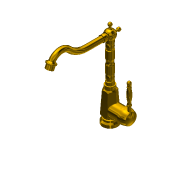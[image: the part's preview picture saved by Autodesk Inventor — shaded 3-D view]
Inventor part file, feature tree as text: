
AUTODESK INVENTOR PART (.ipt)
format: ipt  version: 2018 (Build 220112000, 112)  size: 729,088 bytes
history: native  units: mm
features: sketch x31, extrude x17, projected_geometry x12, fillet x9, revolve x9, plane x6, chamfer x4, other x3, sweep x1, loft x1
ambient origin geometry x8: Origin, YZ Plane, XZ Plane, XY Plane, X Axis, Y Axis, Z Axis, Center Point
bodies: Solid1 (feature_tree)
feature tree (93):
  sweep  "Sweep1"
  extrude  "Extrusion1"  Depth=35.0mm
  extrude  "Extrusion2"  TaperAngle=0.0deg  [1 undecoded]
  fillet  "Fillet1"  Radius=22.8mm
  chamfer  "Chamfer1"  Distance=13.0mm
  extrude  "Extrusion3"  Depth=3.0mm TaperAngle=0.0deg
  extrude  "Extrusion4"  Depth=3.0mm TaperAngle=45.0deg
  revolve  "Revolution1"  [1 undecoded]
  revolve  "Revolution2"  [1 undecoded]
  plane  "Work Plane2"
  extrude  "Extrusion5"  TaperAngle=90.0deg  [1 undecoded]
  other  "Work Axis1"
  sketch  "Sketch10"  dims[d35=1.0mm d36=2.0mm]
  plane  "Work Plane4"
  extrude  "Extrusion6"  Depth=1.0mm
  other  "Work Axis2"
  revolve  "Revolution3"  [1 undecoded]
  revolve  "Revolution4"  Angle=90.0deg
  revolve  "Revolution5"  [1 undecoded]
  fillet  "Fillet2"  [1 undecoded]
  revolve  "Revolution6"  [1 undecoded]
  fillet  "Fillet3"  [1 undecoded]
  extrude  "Extrusion7"  TaperAngle=90.0deg  [1 undecoded]
  revolve  "Revolution7"  Angle=90.0deg
  fillet  "Fillet4"  Radius=6.0mm
  extrude  "Extrusion8"  Depth=12.0mm
  extrude  "Extrusion13"  Depth=6.0mm
  sketch  "Sketch19"  dims[d57=90.0deg d58=2.0mm]
  plane  "Work Plane5"
  loft  "Loft1"
  chamfer  "Chamfer2"  Distance=1.0mm
  fillet  "Fillet5"  Radius=29.0mm
  extrude  "Extrusion10"  Depth=3.0mm TaperAngle=0.0deg
  extrude  "Extrusion11"  Depth=3.0mm
  extrude  "Extrusion12"  Depth=3.0mm
  chamfer  "Chamfer3"  Distance=42.0mm
  chamfer  "Chamfer4"  Angle=90.0deg  [1 undecoded]
  fillet  "Fillet6"  [1 undecoded]
  extrude  "Extrusion14"  Depth=3.0mm TaperAngle=45.0deg
  fillet  "Fillet7"  Radius=1.0mm
  extrude  "Extrusion15"  Depth=3.0mm
  extrude  "Extrusion16"  Depth=10.0mm TaperAngle=0.0deg
  other  "Work Axis3"
  sketch  "Sketch28"  dims[d70=30.0mm]
  plane  "Work Plane6"
  revolve  "Revolution8"  [1 undecoded]
  revolve  "Revolution9"  [1 undecoded]
  extrude  "Extrusion17"  Depth=3.0mm
  fillet  "Fillet8"  Radius=13.0mm
  fillet  "Fillet9"  Radius=6.5mm
  extrude  "Extrusion18"  Depth=3.0mm TaperAngle=45.0deg
  sketch  "Sketch1"  dims[d0=50.0mm d1=15.0mm]
  sketch  "Sketch2"  dims[d5=170.0mm d10=35.0mm]
  sketch  "Sketch3"  dims[d11=17.5mm d12=0.0mm d13=0.0mm d14=22.8mm d15=13.0mm d16=0.0mm]
  sketch  "Sketch4"  dims[d17=3.0mm d18=5.0mm d19=0.0mm]
  sketch  "Sketch5"  dims[d20=2.0mm d21=3.0mm d22=2.0mm d23=45.0deg]
  projected_geometry  "Projected Loop1"
  sketch  "Sketch6"  dims[d24=1.0mm d25=5.0mm d26=0.0mm]
  sketch  "Sketch7"  dims[d27=23.0mm d28=16.0mm d29=0.0mm]
  projected_geometry  "Projected Loop2"
  sketch  "Sketch8"  dims[d30=2.0mm d32=90.0deg]
  plane  "Work Plane1"
  sketch  "Sketch9"  dims[d33=2.0mm d34=1.0mm]
  plane  "Work Plane3"
  sketch  "Sketch11"  dims[d37=32.0mm d38=90.0deg]
  sketch  "Sketch12"  dims[d39=-2.0mm d40=16.0mm d41=0.0mm d42=0.0mm]
  projected_geometry  "Projected Loop3"
  projected_geometry  "Projected Loop4"
  sketch  "Sketch13"  dims[d43=12.0mm d44=28.0mm d46=-30.0mm]
  sketch  "Sketch14"  dims[d47=16.0mm d48=0.0mm d49=90.0deg]
  projected_geometry  "Projected Loop5"
  projected_geometry  "Projected Loop6"
  sketch  "Sketch15"  dims[d50=1.0mm d51=90.0deg d52=6.0mm]
  sketch  "Sketch16"  dims[d53=0.0mm d54=12.0mm]
  projected_geometry  "Projected Loop7"
  sketch  "Sketch17"  dims[d55=28.0mm d56=6.0mm]
  sketch  "Sketch20"  dims[d59=1.0mm]
  sketch  "Sketch21"  dims[d60=90.0deg]
  sketch  "Sketch22"  dims[d61=1.0mm]
  projected_geometry  "Projected Loop9"
  sketch  "Sketch23"  dims[d62=23.0mm]
  sketch  "Sketch24"  dims[d63=125.0mm d64=8.0mm d65=0.0mm d66=0.0mm]
  projected_geometry  "Projected Loop10"
  sketch  "Sketch25"  dims[d67=18.0mm]
  sketch  "Sketch26"  dims[d68=16.0mm]
  projected_geometry  "Projected Loop11"
  sketch  "Sketch27"  dims[d69=2.0mm]
  sketch  "Sketch29"  dims[d71=10.0mm]
  sketch  "Sketch30"  dims[d72=20.0mm]
  sketch  "Sketch31"  dims[d73=2.0mm]
  projected_geometry  "Projected Loop12"
  sketch  "Sketch32"  dims[d74=90.0deg d75=1.0mm d76=29.0mm d77=16.0mm d78=0.0mm d85=34.0mm d86=65.0mm d87=42.0mm d88=0.0mm d89=90.0deg d90=0.0mm d91=90.0deg d92=5.0mm d93=2.0mm d94=45.0deg d95=1.0mm d96=35.0mm d97=10.0mm d98=0.0mm d99=40.0mm d100=6.0mm d101=0.0mm d102=48.0mm d103=13.0mm d104=0.0mm d105=6.5mm d106=2.0mm d107=45.0deg d108=4.0mm d109=2.0mm d110=45.0deg d111=1.5mm d112=1.0mm d113=5.0mm d114=1.0mm d115=5.0mm d116=0.0mm d117=0.0mm d118=40.0mm d119=41.0mm d120=0.0mm d121=2.0mm d122=1.0mm d123=0.1mm d124=0.0mm d125=4.0mm d126=0.0mm d127=23.0mm d128=23.0mm d129=18.5mm d130=7.0mm d131=50.0mm d132=50.0mm d133=90.0deg d134=83.0mm d135=12.0mm d136=4.6mm d137=7.2mm d138=36.0mm d139=9.0mm d140=5.0mm d141=20.0mm d142=5.6mm d143=13.0mm d144=5.0mm d145=90.0deg d146=10.0mm d147=0.0mm d148=1.0mm d149=3.0mm d150=9.0mm d151=25.0mm d152=0.0mm]
  projected_geometry  "Projected Loop13"
note: 14 required parameter values undecoded (feature->parameter linkage not recoverable at this tier; creation-order binding heuristic only, values carry confidence <= 0.55)